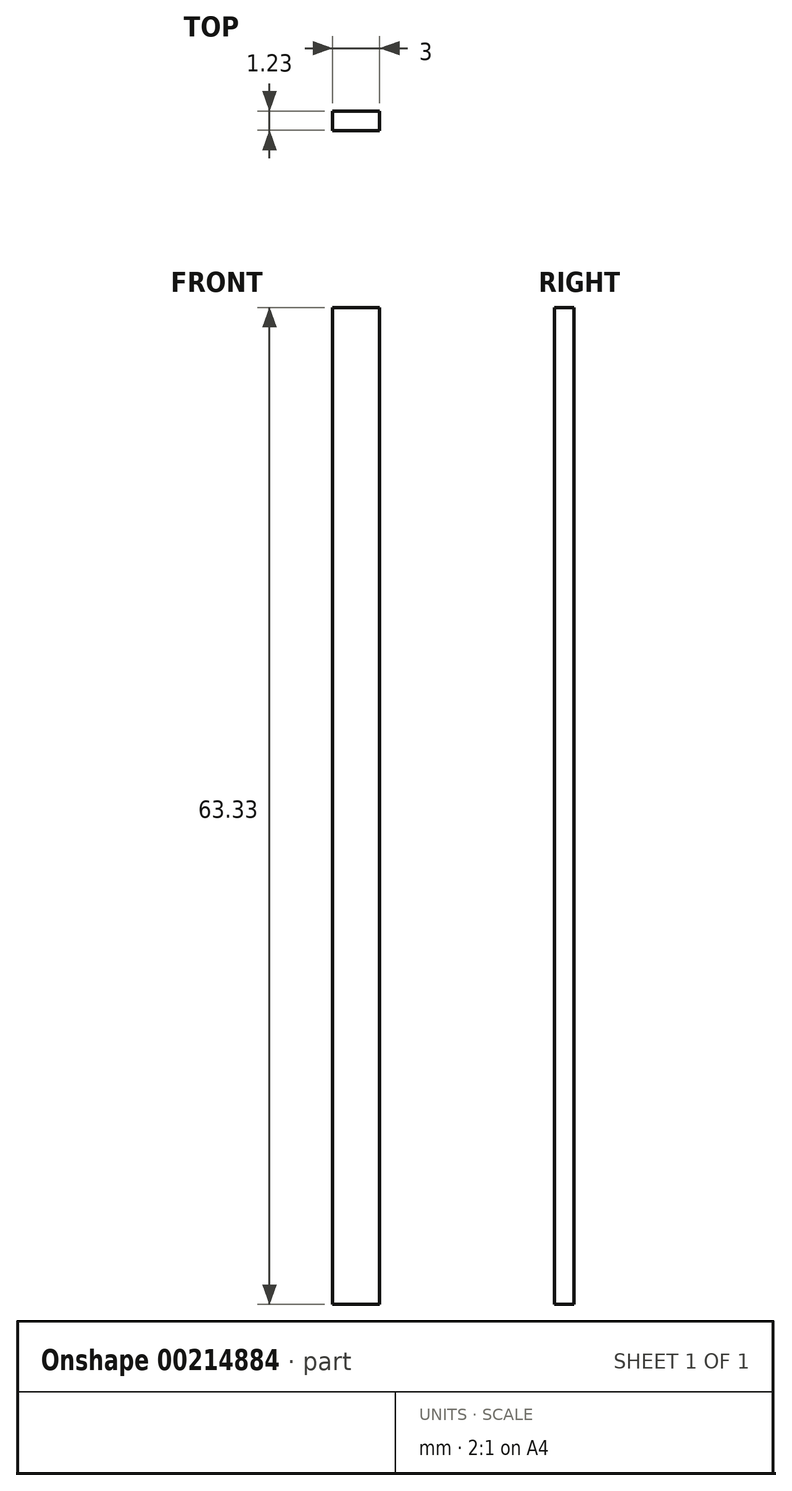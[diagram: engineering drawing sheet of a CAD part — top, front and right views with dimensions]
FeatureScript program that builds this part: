
annotation { "Feature Type Name" : "Feature", "Feature Type Description" : "" }
export const myFeature = defineFeature(function(context is Context, id is Id, definition is map)
    precondition{}
    {
        {
            var Q0;
            Q0=qCreatedBy(makeId("Top.planeOp"),FACE);
            var sketch = newSketch(context, id + "F2", { "sketchPlane" : qUnion([Q0])});
            skLineSegment(sketch, "E0.bottom", {"start": v(0, 0) * mm, "end": v(3, 0) * mm});
            skLineSegment(sketch, "E0.top", {"start": v(0, -1.23) * mm, "end": v(3, -1.23) * mm});
            skLineSegment(sketch, "E0.left", {"start": v(0, 0) * mm, "end": v(0, -1.23) * mm});
            skLineSegment(sketch, "E0.right", {"start": v(3, 0) * mm, "end": v(3, -1.23) * mm});
            skSolve(sketch);
        }
        {
            var Q0;
            Q0=makeQuery(id+"F2.imprint","IMPRINT",FACE,{"disambiguationData":[TD([[makeQuery(id+"F2.imprint","IMPRINT",EDGE,{"derivedFrom":sQuery(id+"F2.wireOp",EDGE,"E0.bottom")}),-1.0]])]});
            extrude(context, id + "F3", {"entities" : qUnion([Q0]), "depth" : 37.93 * mm});
        }
        {
            var Q0;
            Q0=makeQuery(id+"F3.opExtrude","CAP_FACE",FACE,{"disambiguationData":[OSD([sQuery(id+"F2.wireOp",EDGE,"E0.bottom"),sQuery(id+"F2.wireOp",EDGE,"E0.top"),sQuery(id+"F2.wireOp",EDGE,"E0.left"),sQuery(id+"F2.wireOp",EDGE,"E0.right")])],"isStart":false});
            extrude(context, id + "F0", {"entities" : qUnion([Q0]), "operationType" : NewBodyOperationType.ADD, "depth" : 25.4 * mm});
        }
    });
